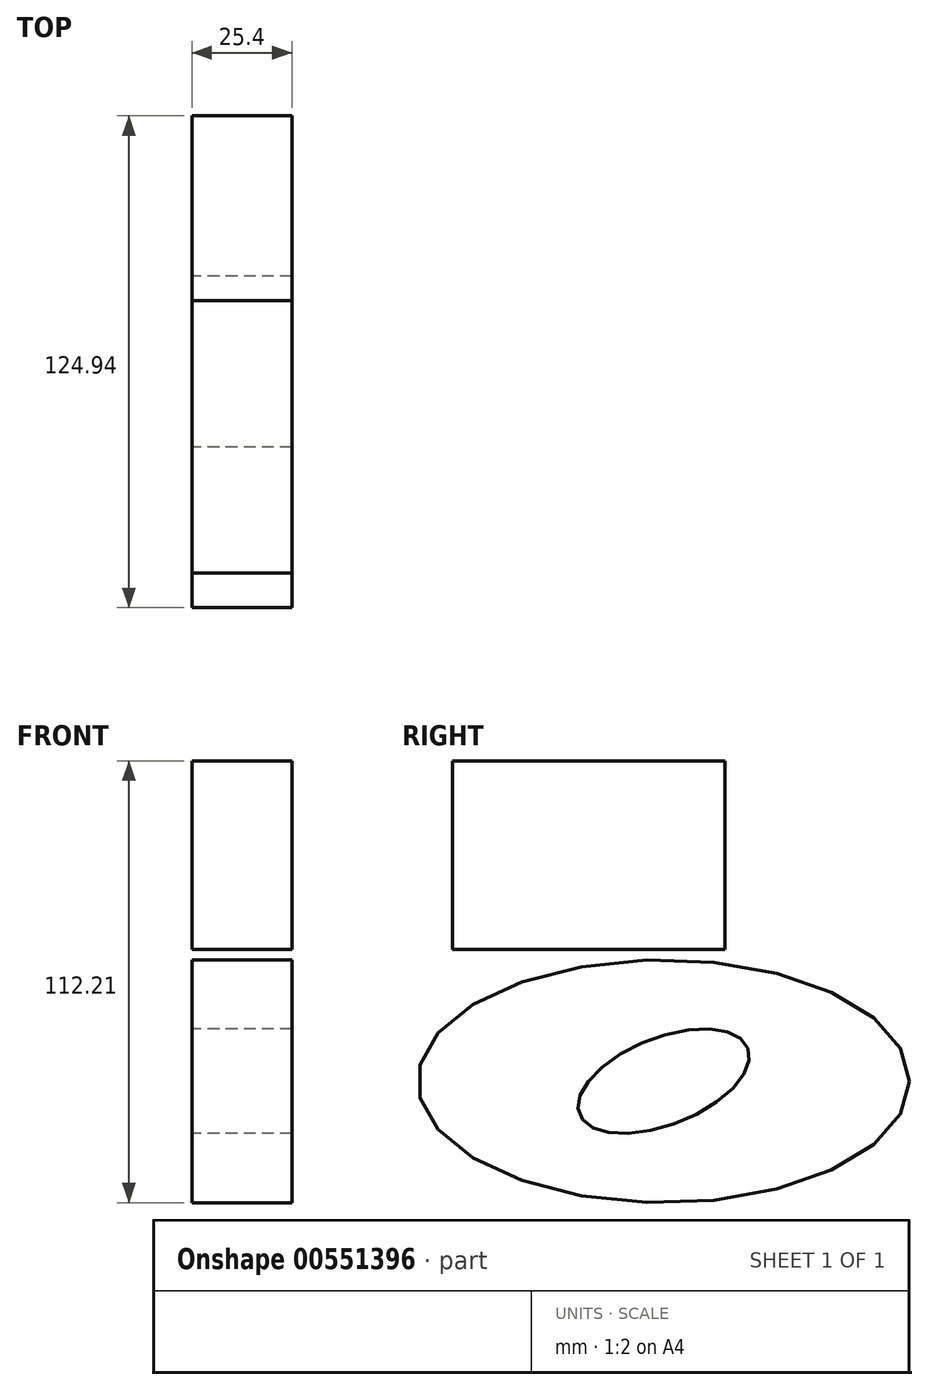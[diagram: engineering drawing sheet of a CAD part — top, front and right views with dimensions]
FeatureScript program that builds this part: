
annotation { "Feature Type Name" : "Feature", "Feature Type Description" : "" }
export const myFeature = defineFeature(function(context is Context, id is Id, definition is map)
    precondition{}
    {
        {
            var Q0;
            Q0=qCreatedBy(makeId("Right.planeOp"),FACE);
            var sketch = newSketch(context, id + "F0", { "sketchPlane" : qUnion([Q0])});
            skLineSegment(sketch, "E0.bottom", {"start": v(15.56, 47.83) * mm, "end": v(-53.69, 47.83) * mm});
            skLineSegment(sketch, "E0.top", {"start": v(15.56, 0) * mm, "end": v(-53.69, 0) * mm});
            skLineSegment(sketch, "E0.left", {"start": v(15.56, 47.83) * mm, "end": v(15.56, 0) * mm});
            skLineSegment(sketch, "E0.right", {"start": v(-53.69, 47.83) * mm, "end": v(-53.69, 0) * mm});
            skSolve(sketch);
        }
        {
            var Q0;
            Q0=makeQuery(id+"F0.imprint","IMPRINT",FACE,{"disambiguationData":[TD([[makeQuery(id+"F0.imprint","IMPRINT",EDGE,{"derivedFrom":sQuery(id+"F0.wireOp",EDGE,"E0.bottom")}),1.0]])]});
            extrude(context, id + "F1", {"entities" : qUnion([Q0]), "depth" : 25.4 * mm, "offsetDistance" : 25.4 * mm});
        }
        {
            var Q0;
            Q0=qCreatedBy(makeId("Right.planeOp"),FACE);
            var sketch = newSketch(context, id + "F2", { "sketchPlane" : qUnion([Q0])});
            skEllipse(sketch, "E1", {"center": v(0, -33.52) * mm, "majorRadius": 62.47 * mm, "minorRadius": 30.85 * mm, "majorAxis": v(1, 0)});
            skEllipse(sketch, "E2", {"center": v(0, -33.52) * mm, "majorRadius": 22.96 * mm, "minorRadius": 11.07 * mm, "majorAxis": v(0.93, 0.37)});
            skSolve(sketch);
        }
        {
            var Q0;
            Q0 = qSketchRegion(id + "F2", true);
            extrude(context, id + "F3", {"entities" : qUnion([Q0]), "depth" : 25.4 * mm, "offsetDistance" : 25.4 * mm});
        }
    });
